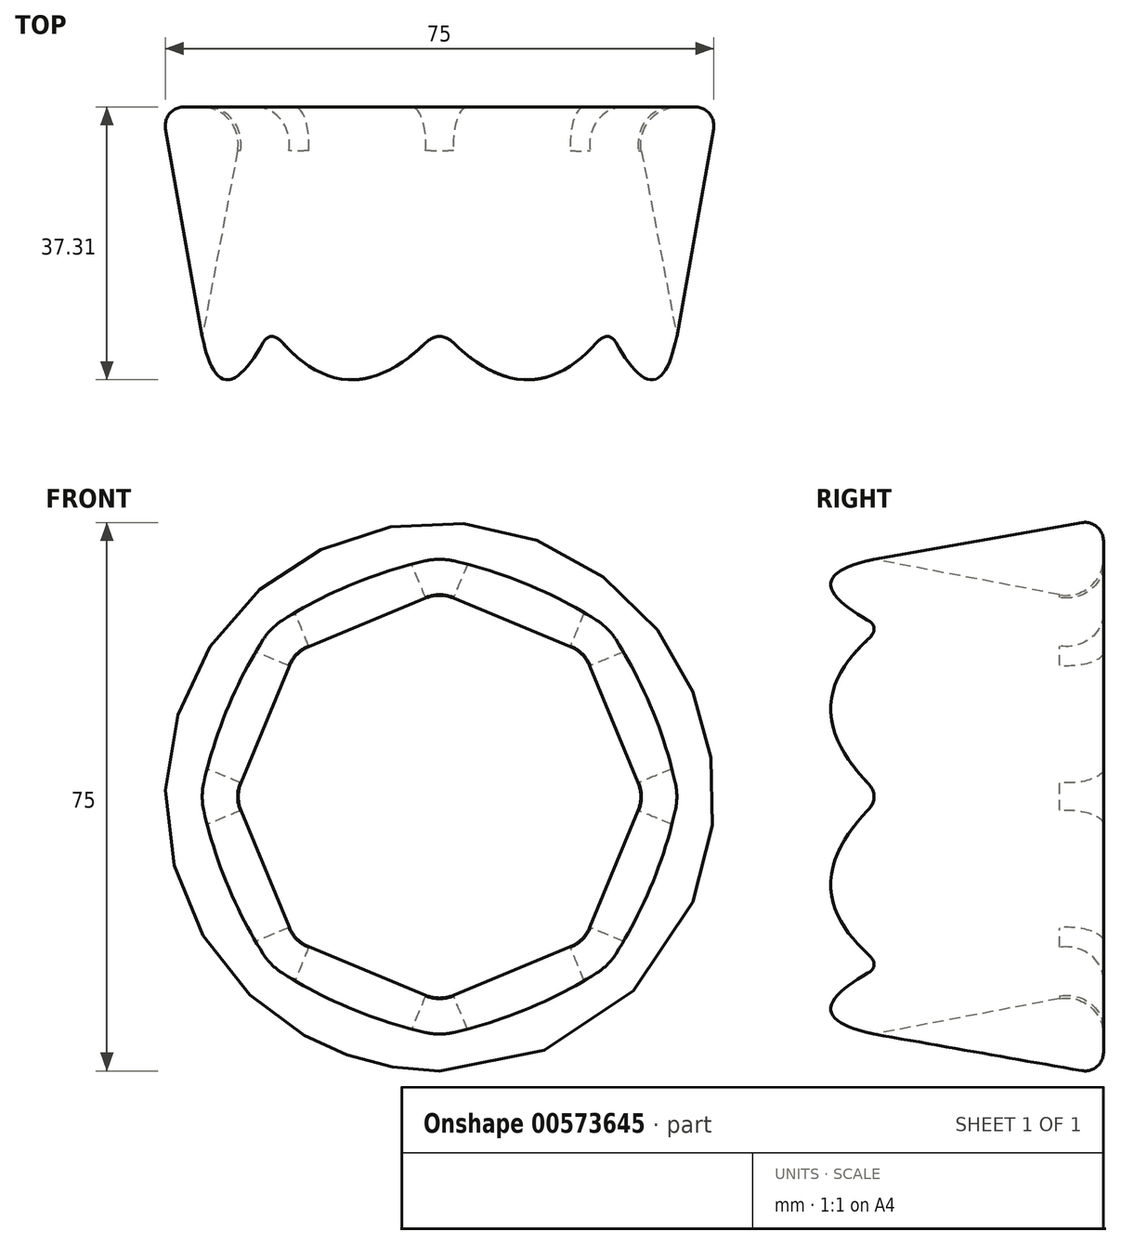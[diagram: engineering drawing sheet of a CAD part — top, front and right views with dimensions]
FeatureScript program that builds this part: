
annotation { "Feature Type Name" : "Feature", "Feature Type Description" : "" }
export const myFeature = defineFeature(function(context is Context, id is Id, definition is map)
    precondition{}
    {
        {
            var Q0;
            Q0=qCreatedBy(makeId("Front.planeOp"),FACE);
            var sketch = newSketch(context, id + "F0", { "sketchPlane" : qUnion([Q0])});
            skCircle(sketch, "E0", {"center": v(0, 0) * mm, "radius": 38 * mm});
            skLineSegment(sketch, "E1.bottom", {"start": v(-1.34, -26.85) * mm, "end": v(1.34, -26.85) * mm});
            skLineSegment(sketch, "E1.top", {"start": v(-1.34, 26.85) * mm, "end": v(1.34, 26.85) * mm});
            skCircle(sketch, "E2.cCircle", {"center": v(0, 0) * mm, "radius": 26.88 * mm, "construction": true});
            skLineSegment(sketch, "E2.0", {"start": v(-26.88, 0) * mm, "end": v(-19, 19) * mm});
            skLineSegment(sketch, "E2.1", {"start": v(-19, 19) * mm, "end": v(0, 26.88) * mm});
            skLineSegment(sketch, "E2.2", {"start": v(0, 26.88) * mm, "end": v(19, 19) * mm});
            skLineSegment(sketch, "E2.3", {"start": v(19, 19) * mm, "end": v(26.88, 0) * mm});
            skLineSegment(sketch, "E2.4", {"start": v(26.88, 0) * mm, "end": v(19, -19) * mm});
            skLineSegment(sketch, "E2.5", {"start": v(19, -19) * mm, "end": v(0, -26.88) * mm});
            skLineSegment(sketch, "E2.6", {"start": v(0, -26.88) * mm, "end": v(-19, -19) * mm});
            skLineSegment(sketch, "E2.7", {"start": v(-19, -19) * mm, "end": v(-26.88, 0) * mm});
            skPoint(sketch, "E3.orphan", {"position": v(26.88, 26.85) * mm});
            skPoint(sketch, "E4.orphan", {"position": v(26.88, -26.85) * mm});
            skPoint(sketch, "E5.orphan", {"position": v(-26.88, -26.85) * mm});
            skPoint(sketch, "E1.left.end.orphan", {"position": v(-26.88, 26.85) * mm});
            skSolve(sketch);
        }
        {
            var Q0;
            Q0 = qSketchRegion(id + "F0", true);
            extrude(context, id + "F1", {"entities" : qUnion([Q0]), "depth" : 101.6 * mm, "offsetDistance" : 25.4 * mm, "hasDraft" : true, "draftAngle" : 10 * degree, "draftPullDirection" : true});
        }
        {
            var Q0;
            Q0=makeQuery(id+"F1.opExtrude","SWEPT_EDGE",EDGE,{"disambiguationData":[OSD([sQuery(id+"F0.wireOp",EDGE,"E2.3"),sQuery(id+"F0.wireOp",EDGE,"E2.4")])]});
            var Q1;
            Q1=makeQuery(id+"F1.opExtrude","SWEPT_EDGE",EDGE,{"disambiguationData":[OSD([sQuery(id+"F0.wireOp",EDGE,"E2.4"),sQuery(id+"F0.wireOp",EDGE,"E2.5")])]});
            var Q2;
            Q2=makeQuery(id+"F1.opExtrude","SWEPT_EDGE",EDGE,{"disambiguationData":[OSD([sQuery(id+"F0.wireOp",EDGE,"E2.2"),sQuery(id+"F0.wireOp",EDGE,"E2.3")])]});
            var Q3;
            Q3=makeQuery(id+"F1.opExtrude","SWEPT_EDGE",EDGE,{"disambiguationData":[OSD([sQuery(id+"F0.wireOp",EDGE,"E2.1"),sQuery(id+"F0.wireOp",EDGE,"E2.2")])]});
            var Q4;
            Q4=makeQuery(id+"F1.opExtrude","SWEPT_EDGE",EDGE,{"disambiguationData":[OSD([sQuery(id+"F0.wireOp",EDGE,"E2.0"),sQuery(id+"F0.wireOp",EDGE,"E2.1")])]});
            var Q5;
            Q5=makeQuery(id+"F1.opExtrude","SWEPT_EDGE",EDGE,{"disambiguationData":[OSD([sQuery(id+"F0.wireOp",EDGE,"E2.0"),sQuery(id+"F0.wireOp",EDGE,"E2.7")])]});
            var Q6;
            Q6=makeQuery(id+"F1.opExtrude","SWEPT_EDGE",EDGE,{"disambiguationData":[OSD([sQuery(id+"F0.wireOp",EDGE,"E2.6"),sQuery(id+"F0.wireOp",EDGE,"E2.7")])]});
            var Q7;
            Q7=makeQuery(id+"F1.opExtrude","SWEPT_EDGE",EDGE,{"disambiguationData":[OSD([sQuery(id+"F0.wireOp",EDGE,"E2.5"),sQuery(id+"F0.wireOp",EDGE,"E2.6")])]});
            fillet(context, id + "F2", {"entities" : qUnion([Q0, Q1, Q2, Q3, Q4, Q5, Q6, Q7]), "radius" : 5.08 * mm, "tangentPropagation" : true, "allowEdgeOverflow" : false});
        }
        {
            var Q0;
            Q0=makeQuery(id+"F1.opExtrude","CAP_EDGE",EDGE,{"disambiguationData":[OSD([sQuery(id+"F0.wireOp",EDGE,"E2.2")])],"isStart":true});
            fillet(context, id + "F3", {"entities" : qUnion([Q0]), "radius" : 5.08 * mm, "tangentPropagation" : true, "allowEdgeOverflow" : false});
        }
        {
            var Q0;
            Q0=makeQuery(id+"F1.opExtrude","CAP_EDGE",EDGE,{"disambiguationData":[OSD([sQuery(id+"F0.wireOp",EDGE,"E0")])],"isStart":true});
            fillet(context, id + "F4", {"entities" : qUnion([Q0]), "radius" : 2.54 * mm, "tangentPropagation" : true, "allowEdgeOverflow" : false});
        }
    });
